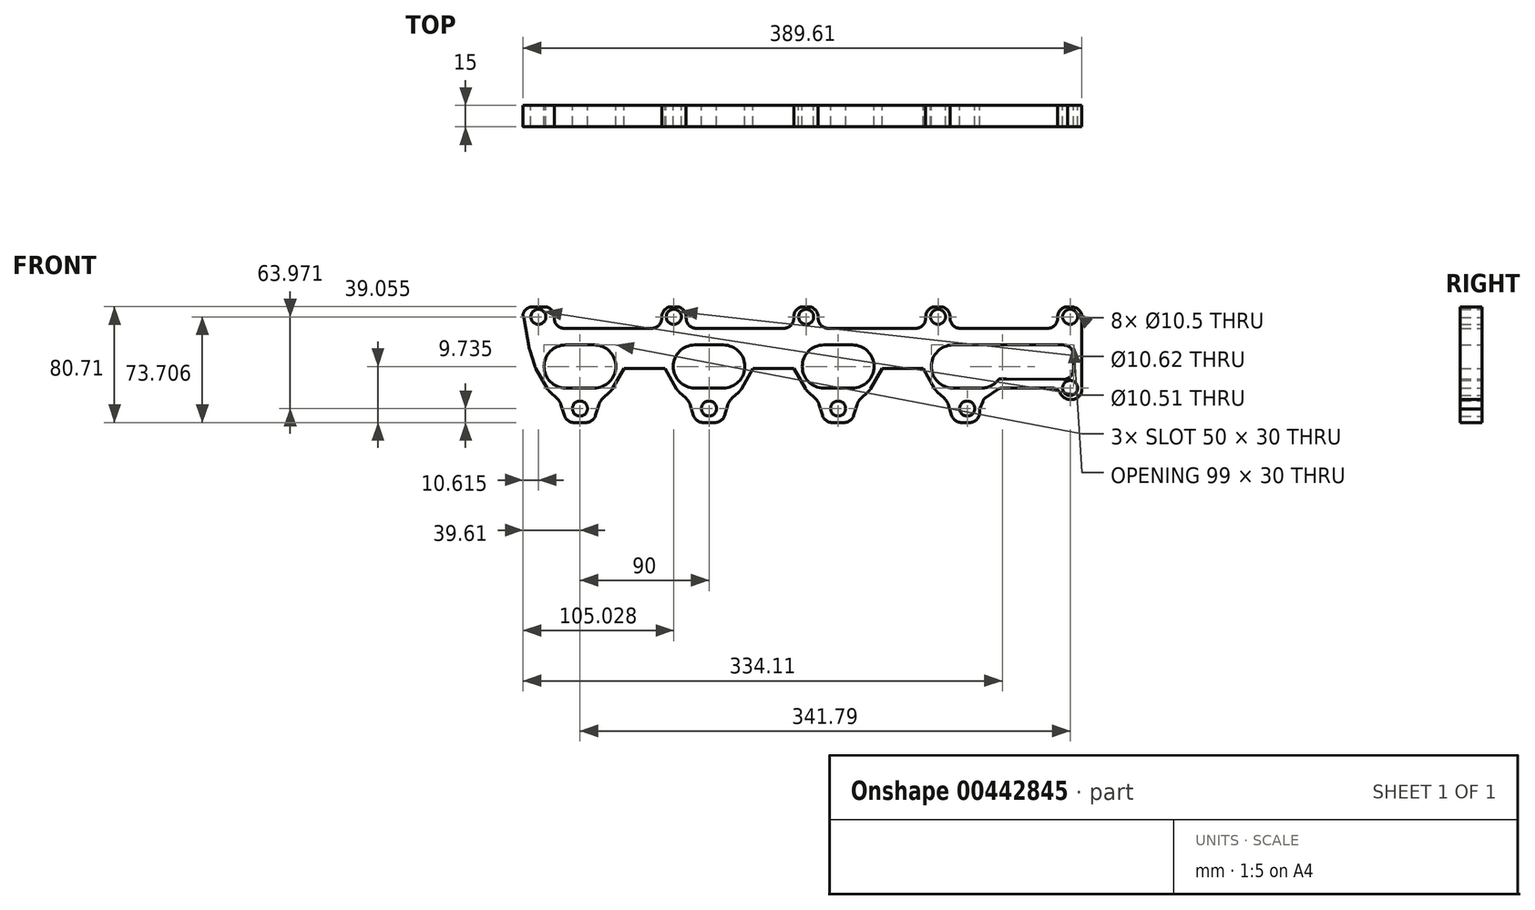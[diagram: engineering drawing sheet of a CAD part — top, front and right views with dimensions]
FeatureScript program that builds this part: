
annotation { "Feature Type Name" : "Feature", "Feature Type Description" : "" }
export const myFeature = defineFeature(function(context is Context, id is Id, definition is map)
    precondition{}
    {
        {
            var Q0;
            Q0=qCreatedBy(makeId("Front.planeOp"),FACE);
            var sketch = newSketch(context, id + "F0", { "sketchPlane" : qUnion([Q0])});
            skLineSegment(sketch, "E0", {"start": v(195, 73.48) * mm, "end": v(195, 23.07) * mm});
            skLineSegment(sketch, "E1", {"start": v(0, 0) * mm, "end": v(0, 80) * mm});
            skLineSegment(sketch, "E2", {"start": v(0, 40) * mm, "end": v(195, 40) * mm, "construction": true});
            skLineSegment(sketch, "E3", {"start": v(195, 40) * mm, "end": v(189, 40) * mm, "construction": true});
            skLineSegment(sketch, "E4", {"start": v(189, 40) * mm, "end": v(189, 47.06) * mm, "construction": true});
            skLineSegment(sketch, "E5", {"start": v(189, 40) * mm, "end": v(189, 0) * mm, "construction": true});
            skLineSegment(sketch, "E6", {"start": v(189, 80) * mm, "end": v(189, 55) * mm, "construction": true});
            skLineSegment(sketch, "E7", {"start": v(189, 47.06) * mm, "end": v(189, 37) * mm, "construction": true});
            skLineSegment(sketch, "E8", {"start": v(189, 55) * mm, "end": v(189, 30) * mm});
            skPoint(sketch, "E9.visualSharp", {"position": v(189, 55) * mm});
            skPoint(sketch, "E10.visualSharp", {"position": v(189, 30) * mm});
            skArc(sketch, "E10.filletArc", {"start": v(184.06, 30.3) * mm, "mid": v(187.63, 32.84) * mm, "end": v(189, 37) * mm});
            skPoint(sketch, "E11.visualSharp", {"position": v(182, 30) * mm});
            skArc(sketch, "E11.filletArc", {"start": v(182, 30) * mm, "mid": v(183.04, 30.08) * mm, "end": v(184.06, 30.3) * mm});
            skLineSegment(sketch, "E12", {"start": v(182, 30) * mm, "end": v(142.46, 30.27) * mm});
            skPoint(sketch, "E13.visualSharp", {"position": v(137.43, 30.3) * mm});
            skPoint(sketch, "E14.midSnap0", {"position": v(97.5, 40) * mm});
            skLineSegment(sketch, "E15", {"start": v(97.5, 40) * mm, "end": v(60.07, 40) * mm, "construction": true});
            skLineSegment(sketch, "E16", {"start": v(15, 54.06) * mm, "end": v(35, 54.06) * mm});
            skLineSegment(sketch, "E17", {"start": v(35, 24.06) * mm, "end": v(15, 24.06) * mm});
            skLineSegment(sketch, "E18", {"start": v(0, 39.06) * mm, "end": v(0, 39.06) * mm});
            skPoint(sketch, "E19.visualSharp", {"position": v(0, 54.06) * mm});
            skPoint(sketch, "E20.visualSharp", {"position": v(0, 24.06) * mm});
            skLineSegment(sketch, "E21", {"start": v(50, 39.06) * mm, "end": v(50, 39.06) * mm});
            skLineSegment(sketch, "E22", {"start": v(60.07, 40) * mm, "end": v(97.5, 40) * mm, "construction": true});
            skArc(sketch, "E23.filletArc", {"start": v(15, 54.06) * mm, "mid": v(4.4, 49.66) * mm, "end": v(0, 39.06) * mm});
            skPoint(sketch, "E24.visualSharp", {"position": v(50, 54.06) * mm});
            skArc(sketch, "E24.filletArc", {"start": v(50, 39.06) * mm, "mid": v(45.6, 49.66) * mm, "end": v(35, 54.06) * mm});
            skPoint(sketch, "E25.visualSharp", {"position": v(50, 24.06) * mm});
            skArc(sketch, "E25.filletArc", {"start": v(35, 24.06) * mm, "mid": v(45.6, 28.45) * mm, "end": v(50, 39.06) * mm});
            skArc(sketch, "E26.filletArc", {"start": v(0, 39.06) * mm, "mid": v(4.4, 28.45) * mm, "end": v(15, 24.06) * mm});
            skLineSegment(sketch, "E27.1.0.0", {"start": v(-75, 54.06) * mm, "end": v(-55, 54.06) * mm});
            skArc(sketch, "E27.1.0.1", {"start": v(-75, 54.06) * mm, "mid": v(-85.6, 49.66) * mm, "end": v(-90, 39.06) * mm});
            skLineSegment(sketch, "E27.1.0.2", {"start": v(-90, 39.06) * mm, "end": v(-90, 39.06) * mm});
            skArc(sketch, "E27.1.0.3", {"start": v(-90, 39.06) * mm, "mid": v(-85.6, 28.45) * mm, "end": v(-75, 24.06) * mm});
            skLineSegment(sketch, "E27.1.0.4", {"start": v(-55, 24.06) * mm, "end": v(-75, 24.06) * mm});
            skLineSegment(sketch, "E27.1.0.5", {"start": v(-40, 39.06) * mm, "end": v(-40, 39.06) * mm});
            skArc(sketch, "E27.1.0.6", {"start": v(-40, 39.06) * mm, "mid": v(-44.4, 49.66) * mm, "end": v(-55, 54.06) * mm});
            skArc(sketch, "E27.1.0.7", {"start": v(-55, 24.06) * mm, "mid": v(-44.4, 28.45) * mm, "end": v(-40, 39.06) * mm});
            skLineSegment(sketch, "E27.2.0.0", {"start": v(-165, 54.06) * mm, "end": v(-145, 54.06) * mm});
            skArc(sketch, "E27.2.0.1", {"start": v(-165, 54.06) * mm, "mid": v(-175.6, 49.66) * mm, "end": v(-180, 39.06) * mm});
            skLineSegment(sketch, "E27.2.0.2", {"start": v(-180, 39.06) * mm, "end": v(-180, 39.06) * mm});
            skArc(sketch, "E27.2.0.3", {"start": v(-180, 39.06) * mm, "mid": v(-175.6, 28.45) * mm, "end": v(-165, 24.06) * mm});
            skLineSegment(sketch, "E27.2.0.4", {"start": v(-145, 24.06) * mm, "end": v(-165, 24.06) * mm});
            skLineSegment(sketch, "E27.2.0.5", {"start": v(-130, 39.06) * mm, "end": v(-130, 39.06) * mm});
            skArc(sketch, "E27.2.0.6", {"start": v(-130, 39.06) * mm, "mid": v(-134.4, 49.66) * mm, "end": v(-145, 54.06) * mm});
            skArc(sketch, "E27.2.0.7", {"start": v(-145, 24.06) * mm, "mid": v(-134.4, 28.45) * mm, "end": v(-130, 39.06) * mm});
            skLineSegment(sketch, "E27.direction1", {"start": v(15, 54.06) * mm, "end": v(-75, 54.06) * mm, "construction": true});
            skArc(sketch, "E28.1.0.1", {"start": v(105, 54.06) * mm, "mid": v(94.4, 49.66) * mm, "end": v(90, 39.06) * mm});
            skArc(sketch, "E28.1.0.2", {"start": v(90, 39.06) * mm, "mid": v(94.4, 28.45) * mm, "end": v(105, 24.06) * mm});
            skLineSegment(sketch, "E28.1.0.3", {"start": v(125, 24.06) * mm, "end": v(105, 24.06) * mm});
            skArc(sketch, "E28.1.0.4", {"start": v(125, 24.06) * mm, "mid": v(131.7, 25.63) * mm, "end": v(136.99, 30.04) * mm});
            skLineSegment(sketch, "E28.1.0.5", {"start": v(105, 54.06) * mm, "end": v(125, 54.06) * mm});
            skLineSegment(sketch, "E28.direction1", {"start": v(35, 39.06) * mm, "end": v(125, 39.06) * mm, "construction": true});
            skLineSegment(sketch, "E29", {"start": v(137.62, 30.35) * mm, "end": v(142.46, 30.27) * mm});
            skLineSegment(sketch, "E30", {"start": v(125, 54.06) * mm, "end": v(182, 54.06) * mm});
            skLineSegment(sketch, "E31", {"start": v(189, 54.06) * mm, "end": v(189, 37) * mm});
            skArc(sketch, "E32.filletArc", {"start": v(189, 47.06) * mm, "mid": v(186.95, 52) * mm, "end": v(182, 54.06) * mm});
            skPoint(sketch, "E33.newPointB", {"position": v(140, 39.06) * mm});
            skArc(sketch, "E33.filletArc", {"start": v(137.62, 30.35) * mm, "mid": v(137.27, 30.27) * mm, "end": v(136.99, 30.04) * mm});
            skLineSegment(sketch, "E34", {"start": v(-173, 0) * mm, "end": v(-194.92, 0.7) * mm, "construction": true});
            skLineSegment(sketch, "E35", {"start": v(-172.92, 73.7) * mm, "end": v(-172.92, 72.7) * mm});
            skLineSegment(sketch, "E36", {"start": v(-165.92, 65.7) * mm, "end": v(-104.92, 65.7) * mm});
            skLineSegment(sketch, "E37", {"start": v(-97.92, 72.7) * mm, "end": v(-97.92, 73.7) * mm});
            skPoint(sketch, "E38.visualSharp", {"position": v(-172.92, 80.7) * mm});
            skArc(sketch, "E38.filletArc", {"start": v(-172.92, 79.93) * mm, "mid": v(-173.15, 80.48) * mm, "end": v(-173.7, 80.7) * mm, "construction": true});
            skLineSegment(sketch, "E39", {"start": v(-194.92, 80.7) * mm, "end": v(-179.92, 80.7) * mm});
            skLineSegment(sketch, "E40", {"start": v(-172.92, 79.93) * mm, "end": v(-172.92, 65.7) * mm});
            skPoint(sketch, "E41.visualSharp", {"position": v(-194.92, 80.7) * mm});
            skArc(sketch, "E41.filletArc", {"start": v(-187.92, 80.7) * mm, "mid": v(-191.62, 79.64) * mm, "end": v(-194.2, 76.78) * mm});
            skArc(sketch, "E42.filletArc", {"start": v(-172.92, 73.7) * mm, "mid": v(-174.97, 78.66) * mm, "end": v(-179.92, 80.7) * mm});
            skPoint(sketch, "E43.visualSharp", {"position": v(-172.92, 65.7) * mm});
            skArc(sketch, "E43.filletArc", {"start": v(-172.92, 72.7) * mm, "mid": v(-170.87, 67.76) * mm, "end": v(-165.92, 65.7) * mm});
            skPoint(sketch, "E44.visualSharp", {"position": v(-97.92, 65.7) * mm});
            skArc(sketch, "E44.filletArc", {"start": v(-104.92, 65.7) * mm, "mid": v(-99.97, 67.76) * mm, "end": v(-97.92, 72.7) * mm});
            skPoint(sketch, "E45.newPointA", {"position": v(-195, 80) * mm});
            skPoint(sketch, "E45.newPointB", {"position": v(-97.92, 80.7) * mm});
            skArc(sketch, "E45.filletArc", {"start": v(-90.92, 80.7) * mm, "mid": v(-95.87, 78.66) * mm, "end": v(-97.92, 73.7) * mm});
            skCircle(sketch, "E46", {"center": v(-184, 73.7) * mm, "radius": 5.25 * mm});
            skLineSegment(sketch, "E47", {"start": v(-155, 0) * mm, "end": v(-155, 24.06) * mm, "construction": true});
            skPoint(sketch, "E47.startSnap0", {"position": v(-155, 24.06) * mm});
            skCircle(sketch, "E48", {"center": v(-155, 9.73) * mm, "radius": 5.25 * mm});
            skPoint(sketch, "E49.newPointA", {"position": v(-195, 0) * mm});
            skPoint(sketch, "E50.newPointA", {"position": v(0, 40) * mm});
            skPoint(sketch, "E51.visualSharp", {"position": v(-87.22, 24.06) * mm});
            skArc(sketch, "E51.filletArc", {"start": v(-87.45, 24.4) * mm, "mid": v(-87.2, 24.07) * mm, "end": v(-86.91, 23.79) * mm});
            skPoint(sketch, "E52.visualSharp", {"position": v(-75.76, 14.1) * mm});
            skArc(sketch, "E52.filletArc", {"start": v(-75.76, 12.8) * mm, "mid": v(-76.02, 13.98) * mm, "end": v(-76.75, 14.96) * mm});
            skLineSegment(sketch, "E53", {"start": v(-65, 24.06) * mm, "end": v(-65, 0) * mm, "construction": true});
            skCircle(sketch, "E54", {"center": v(-65, 9.73) * mm, "radius": 5.25 * mm});
            skLineSegment(sketch, "E55.1.0.0", {"start": v(-73.92, 65.7) * mm, "end": v(-12.92, 65.7) * mm});
            skArc(sketch, "E55.1.0.1", {"start": v(-80.92, 72.7) * mm, "mid": v(-78.87, 67.76) * mm, "end": v(-73.92, 65.7) * mm});
            skArc(sketch, "E55.1.0.2", {"start": v(1.08, 80.7) * mm, "mid": v(-3.87, 78.66) * mm, "end": v(-5.92, 73.7) * mm});
            skArc(sketch, "E55.1.0.3", {"start": v(-80.92, 73.7) * mm, "mid": v(-82.97, 78.66) * mm, "end": v(-87.92, 80.7) * mm});
            skLineSegment(sketch, "E55.1.0.4", {"start": v(-80.92, 73.7) * mm, "end": v(-80.92, 72.7) * mm});
            skArc(sketch, "E55.1.0.5", {"start": v(-12.92, 65.7) * mm, "mid": v(-7.97, 67.76) * mm, "end": v(-5.92, 72.7) * mm});
            skLineSegment(sketch, "E55.1.0.6", {"start": v(-5.92, 72.7) * mm, "end": v(-5.92, 73.7) * mm});
            skLineSegment(sketch, "E55.2.0.0", {"start": v(18.08, 65.7) * mm, "end": v(79.08, 65.7) * mm});
            skArc(sketch, "E55.2.0.1", {"start": v(11.08, 72.7) * mm, "mid": v(13.13, 67.76) * mm, "end": v(18.08, 65.7) * mm});
            skArc(sketch, "E55.2.0.2", {"start": v(93.08, 80.7) * mm, "mid": v(88.13, 78.66) * mm, "end": v(86.08, 73.7) * mm});
            skArc(sketch, "E55.2.0.3", {"start": v(11.08, 73.7) * mm, "mid": v(9.03, 78.66) * mm, "end": v(4.08, 80.7) * mm});
            skLineSegment(sketch, "E55.2.0.4", {"start": v(11.08, 73.7) * mm, "end": v(11.08, 72.7) * mm});
            skArc(sketch, "E55.2.0.5", {"start": v(79.08, 65.7) * mm, "mid": v(84.03, 67.76) * mm, "end": v(86.08, 72.7) * mm});
            skLineSegment(sketch, "E55.2.0.6", {"start": v(86.08, 72.7) * mm, "end": v(86.08, 73.7) * mm});
            skLineSegment(sketch, "E55.3.0.0", {"start": v(110.08, 65.7) * mm, "end": v(171.08, 65.7) * mm});
            skArc(sketch, "E55.3.0.1", {"start": v(103.08, 72.7) * mm, "mid": v(105.13, 67.76) * mm, "end": v(110.08, 65.7) * mm});
            skArc(sketch, "E55.3.0.2", {"start": v(185.08, 80.7) * mm, "mid": v(180.13, 78.66) * mm, "end": v(178.08, 73.7) * mm});
            skArc(sketch, "E55.3.0.3", {"start": v(103.08, 73.7) * mm, "mid": v(101.03, 78.66) * mm, "end": v(96.08, 80.7) * mm});
            skLineSegment(sketch, "E55.3.0.4", {"start": v(103.08, 73.7) * mm, "end": v(103.08, 72.7) * mm});
            skArc(sketch, "E55.3.0.5", {"start": v(171.08, 65.7) * mm, "mid": v(176.03, 67.76) * mm, "end": v(178.08, 72.7) * mm});
            skLineSegment(sketch, "E55.3.0.6", {"start": v(178.08, 72.7) * mm, "end": v(178.08, 73.7) * mm});
            skLineSegment(sketch, "E55.direction1", {"start": v(-165.92, 65.7) * mm, "end": v(-73.92, 65.7) * mm, "construction": true});
            skCircle(sketch, "E56", {"center": v(-89.58, 73.7) * mm, "radius": 5.31 * mm});
            skCircle(sketch, "E57", {"center": v(2.71, 73.7) * mm, "radius": 5.25 * mm});
            skCircle(sketch, "E58", {"center": v(94.71, 73.7) * mm, "radius": 5.25 * mm});
            skLineSegment(sketch, "E59", {"start": v(-90.92, 80.7) * mm, "end": v(-87.92, 80.7) * mm});
            skLineSegment(sketch, "E60", {"start": v(1.08, 80.7) * mm, "end": v(4.08, 80.7) * mm});
            skLineSegment(sketch, "E61", {"start": v(93.08, 80.7) * mm, "end": v(96.08, 80.7) * mm});
            skLineSegment(sketch, "E62", {"start": v(185.08, 80.7) * mm, "end": v(188.5, 80.46) * mm});
            skPoint(sketch, "E63.visualSharp", {"position": v(195, 80) * mm});
            skArc(sketch, "E63.filletArc", {"start": v(195, 73.48) * mm, "mid": v(193.12, 78.25) * mm, "end": v(188.5, 80.46) * mm});
            skLineSegment(sketch, "E64", {"start": v(25, 24.06) * mm, "end": v(25, 0) * mm, "construction": true});
            skCircle(sketch, "E65", {"center": v(25, 9.73) * mm, "radius": 5.25 * mm});
            skLineSegment(sketch, "E66", {"start": v(115, 24.06) * mm, "end": v(115, 0) * mm, "construction": true});
            skCircle(sketch, "E67", {"center": v(115, 9.73) * mm, "radius": 5.25 * mm});
            skCircle(sketch, "E68", {"center": v(186.79, 73.7) * mm, "radius": 5.25 * mm});
            skPoint(sketch, "E68.centerSnap0", {"position": v(186.79, 80.58) * mm});
            skCircle(sketch, "E69", {"center": v(186.79, 24.06) * mm, "radius": 5.25 * mm});
            skLineSegment(sketch, "E70", {"start": v(180, 20.42) * mm, "end": v(180.4, 19.7) * mm});
            skLineSegment(sketch, "E71", {"start": v(186.53, 16.07) * mm, "end": v(188, 16.07) * mm});
            skLineSegment(sketch, "E72", {"start": v(173.86, 24.06) * mm, "end": v(139.73, 24.06) * mm});
            skLineSegment(sketch, "E73", {"start": v(135.86, 22.86) * mm, "end": v(128.35, 17.76) * mm});
            skLineSegment(sketch, "E74", {"start": v(125.8, 14.62) * mm, "end": v(123.68, 9.43) * mm});
            skLineSegment(sketch, "E75", {"start": v(123.68, 9.43) * mm, "end": v(123.68, 7) * mm});
            skPoint(sketch, "E76.visualSharp", {"position": v(178, 24.06) * mm});
            skArc(sketch, "E76.filletArc", {"start": v(180, 20.42) * mm, "mid": v(177.42, 23.08) * mm, "end": v(173.86, 24.06) * mm});
            skPoint(sketch, "E77.visualSharp", {"position": v(182.38, 16.07) * mm});
            skArc(sketch, "E77.filletArc", {"start": v(180.4, 19.7) * mm, "mid": v(182.96, 17.05) * mm, "end": v(186.53, 16.07) * mm});
            skPoint(sketch, "E78.newPointB", {"position": v(195, 0) * mm});
            skArc(sketch, "E78.filletArc", {"start": v(188, 16.07) * mm, "mid": v(192.95, 18.12) * mm, "end": v(195, 23.07) * mm});
            skPoint(sketch, "E79.visualSharp", {"position": v(137.61, 24.06) * mm});
            skArc(sketch, "E79.filletArc", {"start": v(139.73, 24.06) * mm, "mid": v(137.7, 23.75) * mm, "end": v(135.86, 22.86) * mm});
            skPoint(sketch, "E80.visualSharp", {"position": v(126.6, 16.58) * mm});
            skArc(sketch, "E80.filletArc", {"start": v(128.35, 17.76) * mm, "mid": v(126.84, 16.38) * mm, "end": v(125.8, 14.62) * mm});
            skLineSegment(sketch, "E81", {"start": v(-165, 24.06) * mm, "end": v(-165, 0) * mm, "construction": true});
            skLineSegment(sketch, "E82", {"start": v(-145, 24.06) * mm, "end": v(-145, 0) * mm, "construction": true});
            skLineSegment(sketch, "E83", {"start": v(-194.87, 74.52) * mm, "end": v(-194.92, 0.7) * mm});
            skPoint(sketch, "E84.visualSharp", {"position": v(-194.87, 74.52) * mm});
            skArc(sketch, "E84.filletArc", {"start": v(-194.2, 76.78) * mm, "mid": v(-194.6, 74.96) * mm, "end": v(-194.13, 73.16) * mm});
            skLineSegment(sketch, "E85", {"start": v(-175.68, 21.14) * mm, "end": v(-171.07, 16.94) * mm});
            skLineSegment(sketch, "E86", {"start": v(-168.27, 12.56) * mm, "end": v(-165.84, 4.89) * mm});
            skPoint(sketch, "E87.visualSharp", {"position": v(-169.08, 15.12) * mm});
            skArc(sketch, "E87.filletArc", {"start": v(-168.27, 12.56) * mm, "mid": v(-169.38, 14.93) * mm, "end": v(-171.07, 16.94) * mm});
            skArc(sketch, "E88.filletArc", {"start": v(-165.84, 4.89) * mm, "mid": v(-163.3, 1.35) * mm, "end": v(-159.17, 0) * mm});
            skPoint(sketch, "E89.visualSharp", {"position": v(-181.83, 50.48) * mm});
            skLineSegment(sketch, "E90", {"start": v(-194.13, 73.16) * mm, "end": v(-190.18, 51.22) * mm});
            skLineSegment(sketch, "E91", {"start": v(-190.03, 50.6) * mm, "end": v(-186.6, 39.63) * mm});
            skLineSegment(sketch, "E92", {"start": v(-185.72, 37.63) * mm, "end": v(-177.61, 23.55) * mm});
            skPoint(sketch, "E93.visualSharp", {"position": v(-190.12, 50.9) * mm});
            skArc(sketch, "E93.filletArc", {"start": v(-190.18, 51.22) * mm, "mid": v(-190.11, 50.91) * mm, "end": v(-190.03, 50.6) * mm});
            skPoint(sketch, "E94.visualSharp", {"position": v(-186.26, 38.59) * mm});
            skArc(sketch, "E94.filletArc", {"start": v(-186.6, 39.63) * mm, "mid": v(-186.2, 38.6) * mm, "end": v(-185.72, 37.63) * mm});
            skPoint(sketch, "E95.visualSharp", {"position": v(-176.83, 22.2) * mm});
            skArc(sketch, "E95.filletArc", {"start": v(-177.61, 23.55) * mm, "mid": v(-176.74, 22.27) * mm, "end": v(-175.68, 21.14) * mm});
            skLineSegment(sketch, "E96.MirrorCS", {"start": v(-124.28, 37.63) * mm, "end": v(-132.39, 23.55) * mm});
            skLineSegment(sketch, "E97.MirrorCS", {"start": v(-134.32, 21.14) * mm, "end": v(-138.93, 16.94) * mm});
            skArc(sketch, "E98.MirrorCS", {"start": v(-132.39, 23.55) * mm, "mid": v(-133.26, 22.27) * mm, "end": v(-134.32, 21.14) * mm});
            skArc(sketch, "E99.MirrorCS", {"start": v(-141.73, 12.56) * mm, "mid": v(-140.62, 14.93) * mm, "end": v(-138.93, 16.94) * mm});
            skLineSegment(sketch, "E100.MirrorCS", {"start": v(-141.73, 12.56) * mm, "end": v(-144.16, 4.89) * mm});
            skArc(sketch, "E101.MirrorCS", {"start": v(-144.16, 4.89) * mm, "mid": v(-146.7, 1.35) * mm, "end": v(-150.83, 0) * mm});
            skLineSegment(sketch, "E102.1.0.0", {"start": v(-34.28, 37.63) * mm, "end": v(-42.39, 23.55) * mm});
            skArc(sketch, "E102.1.0.1", {"start": v(-42.39, 23.55) * mm, "mid": v(-43.26, 22.27) * mm, "end": v(-44.32, 21.14) * mm});
            skLineSegment(sketch, "E102.1.0.2", {"start": v(-44.32, 21.14) * mm, "end": v(-48.93, 16.94) * mm});
            skArc(sketch, "E102.1.0.3", {"start": v(-51.73, 12.56) * mm, "mid": v(-50.62, 14.93) * mm, "end": v(-48.93, 16.94) * mm});
            skLineSegment(sketch, "E102.1.0.4", {"start": v(-51.73, 12.56) * mm, "end": v(-54.16, 4.89) * mm});
            skArc(sketch, "E102.1.0.5", {"start": v(-54.16, 4.89) * mm, "mid": v(-56.7, 1.35) * mm, "end": v(-60.83, 0) * mm});
            skLineSegment(sketch, "E102.2.0.0", {"start": v(55.72, 37.63) * mm, "end": v(47.61, 23.55) * mm});
            skArc(sketch, "E102.2.0.1", {"start": v(47.61, 23.55) * mm, "mid": v(46.74, 22.27) * mm, "end": v(45.68, 21.14) * mm});
            skLineSegment(sketch, "E102.2.0.2", {"start": v(45.68, 21.14) * mm, "end": v(41.07, 16.94) * mm});
            skArc(sketch, "E102.2.0.3", {"start": v(38.27, 12.56) * mm, "mid": v(39.38, 14.93) * mm, "end": v(41.07, 16.94) * mm});
            skLineSegment(sketch, "E102.2.0.4", {"start": v(38.27, 12.56) * mm, "end": v(35.84, 4.89) * mm});
            skArc(sketch, "E102.2.0.5", {"start": v(35.84, 4.89) * mm, "mid": v(33.3, 1.35) * mm, "end": v(29.17, 0) * mm});
            skLineSegment(sketch, "E102.direction1", {"start": v(-132.39, 23.55) * mm, "end": v(-42.39, 23.55) * mm, "construction": true});
            skLineSegment(sketch, "E103.1.0.0", {"start": v(-95.72, 37.63) * mm, "end": v(-87.61, 23.55) * mm});
            skArc(sketch, "E103.1.0.1", {"start": v(-87.61, 23.55) * mm, "mid": v(-86.74, 22.27) * mm, "end": v(-85.68, 21.14) * mm});
            skLineSegment(sketch, "E103.1.0.2", {"start": v(-85.68, 21.14) * mm, "end": v(-81.07, 16.94) * mm});
            skArc(sketch, "E103.1.0.3", {"start": v(-78.27, 12.56) * mm, "mid": v(-79.38, 14.93) * mm, "end": v(-81.07, 16.94) * mm});
            skLineSegment(sketch, "E103.1.0.4", {"start": v(-78.27, 12.56) * mm, "end": v(-75.84, 4.89) * mm});
            skArc(sketch, "E103.1.0.5", {"start": v(-75.84, 4.89) * mm, "mid": v(-73.3, 1.35) * mm, "end": v(-69.17, 0) * mm});
            skLineSegment(sketch, "E103.2.0.0", {"start": v(-5.72, 37.63) * mm, "end": v(2.39, 23.55) * mm});
            skArc(sketch, "E103.2.0.1", {"start": v(2.39, 23.55) * mm, "mid": v(3.26, 22.27) * mm, "end": v(4.32, 21.14) * mm});
            skLineSegment(sketch, "E103.2.0.2", {"start": v(4.32, 21.14) * mm, "end": v(8.93, 16.94) * mm});
            skArc(sketch, "E103.2.0.3", {"start": v(11.73, 12.56) * mm, "mid": v(10.62, 14.93) * mm, "end": v(8.93, 16.94) * mm});
            skLineSegment(sketch, "E103.2.0.4", {"start": v(11.73, 12.56) * mm, "end": v(14.16, 4.89) * mm});
            skArc(sketch, "E103.2.0.5", {"start": v(14.16, 4.89) * mm, "mid": v(16.7, 1.35) * mm, "end": v(20.83, 0) * mm});
            skLineSegment(sketch, "E103.3.0.0", {"start": v(84.28, 37.63) * mm, "end": v(92.39, 23.55) * mm});
            skArc(sketch, "E103.3.0.1", {"start": v(92.39, 23.55) * mm, "mid": v(93.26, 22.27) * mm, "end": v(94.32, 21.14) * mm});
            skLineSegment(sketch, "E103.3.0.2", {"start": v(94.32, 21.14) * mm, "end": v(98.93, 16.94) * mm});
            skArc(sketch, "E103.3.0.3", {"start": v(101.73, 12.56) * mm, "mid": v(100.62, 14.93) * mm, "end": v(98.93, 16.94) * mm});
            skLineSegment(sketch, "E103.3.0.4", {"start": v(101.73, 12.56) * mm, "end": v(104.16, 4.89) * mm});
            skArc(sketch, "E103.3.0.5", {"start": v(104.16, 4.89) * mm, "mid": v(106.7, 1.35) * mm, "end": v(110.83, 0) * mm});
            skLineSegment(sketch, "E103.direction1", {"start": v(-177.61, 23.55) * mm, "end": v(-87.61, 23.55) * mm, "construction": true});
            skLineSegment(sketch, "E104", {"start": v(-124.28, 37.63) * mm, "end": v(-95.72, 37.63) * mm});
            skLineSegment(sketch, "E105", {"start": v(-34.28, 37.63) * mm, "end": v(-5.72, 37.63) * mm});
            skLineSegment(sketch, "E106", {"start": v(55.72, 37.63) * mm, "end": v(84.28, 37.63) * mm});
            skLineSegment(sketch, "E107", {"start": v(-159.17, 0) * mm, "end": v(-155, 0) * mm});
            skLineSegment(sketch, "E108", {"start": v(-155, 0) * mm, "end": v(-150.83, 0) * mm});
            skLineSegment(sketch, "E109", {"start": v(-69.17, 0) * mm, "end": v(-60.83, 0) * mm});
            skLineSegment(sketch, "E110", {"start": v(20.83, 0) * mm, "end": v(29.17, 0) * mm});
            skLineSegment(sketch, "E111", {"start": v(110.83, 0) * mm, "end": v(116.68, 0) * mm});
            skPoint(sketch, "E112.visualSharp", {"position": v(123.68, 0) * mm});
            skArc(sketch, "E112.filletArc", {"start": v(116.68, 0) * mm, "mid": v(121.63, 2.05) * mm, "end": v(123.68, 7) * mm});
            skPoint(sketch, "E113.middle", {"position": v(-155, 39.06) * mm});
            skPoint(sketch, "E113.middle.positionSnap0", {"position": v(-155, 54.06) * mm});
            skPoint(sketch, "E113.centerSnap0", {"position": v(-155, 54.06) * mm});
            skSolve(sketch);
        }
        {
            var Q0;
            Q0 = qSketchRegion(id + "F0", true);
            extrude(context, id + "F1", {"entities" : qUnion([Q0]), "depth" : 15 * mm, "offsetDistance" : 25 * mm});
        }
    });
